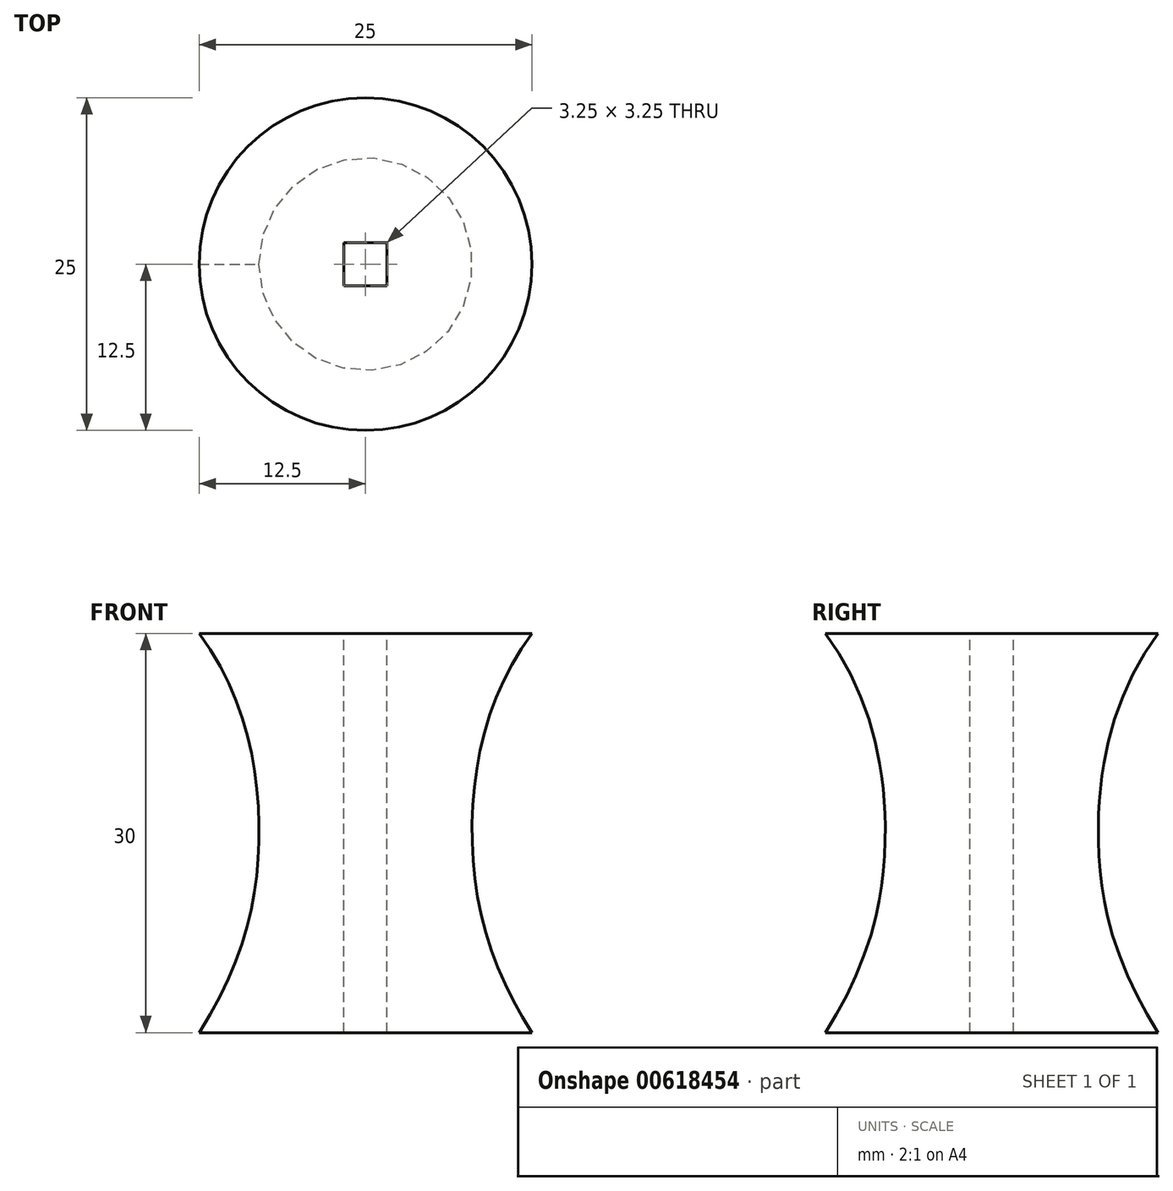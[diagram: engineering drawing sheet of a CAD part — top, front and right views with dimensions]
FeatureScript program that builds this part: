
annotation { "Feature Type Name" : "Feature", "Feature Type Description" : "" }
export const myFeature = defineFeature(function(context is Context, id is Id, definition is map)
    precondition{}
    {
        {
            var Q0;
            Q0=qCreatedBy(makeId("Front.planeOp"),FACE);
            var sketch = newSketch(context, id + "F0", { "sketchPlane" : qUnion([Q0])});
            skLineSegment(sketch, "E0", {"start": v(0, 0) * mm, "end": v(12.5, 0) * mm});
            skLineSegment(sketch, "E1", {"start": v(0, 0) * mm, "end": v(0, 30) * mm});
            skLineSegment(sketch, "E2", {"start": v(0, 30) * mm, "end": v(12.5, 30) * mm});
            skFitSpline(sketch, "E3", {"points": [v(12.5, 30) * mm, v(8, 15) * mm, v(12.5, 0) * mm], "startDerivative": vector(-20.66, -27.96) * mm, "endDerivative": vector(20.23, -32) * mm});
            skSolve(sketch);
        }
        {
            var Q0;
            Q0=makeQuery(id+"F0.imprint","IMPRINT",FACE,{"disambiguationData":[TD([[makeQuery(id+"F0.imprint","IMPRINT",EDGE,{"derivedFrom":sQuery(id+"F0.wireOp",EDGE,"E0")}),1.0]])]});
            var Q1;
            Q1=sQuery(id+"F0.wireOp",EDGE,"E1");
            revolve(context, id + "F1", {"entities" : qUnion([Q0]), "axis" : qUnion([Q1]), "revolveType" : RevolveType.FULL});
        }
        {
            var Q0;
            Q0=makeQuery(id+"F1.opRevolve","SWEPT_FACE",FACE,{"disambiguationData":[OSD([sQuery(id+"F0.wireOp",EDGE,"E2")])]});
            var sketch = newSketch(context, id + "F2", { "sketchPlane" : qUnion([Q0])});
            skLineSegment(sketch, "E4.bottom", {"start": v(1.63, -1.62) * mm, "end": v(-1.63, -1.63) * mm});
            skLineSegment(sketch, "E4.top", {"start": v(1.63, 1.63) * mm, "end": v(-1.62, 1.63) * mm});
            skLineSegment(sketch, "E4.left", {"start": v(1.63, -1.62) * mm, "end": v(1.63, 1.63) * mm});
            skLineSegment(sketch, "E4.right", {"start": v(-1.62, -1.63) * mm, "end": v(-1.62, 1.63) * mm});
            skPoint(sketch, "E4.middle", {"position": v(0, 0) * mm});
            skSolve(sketch);
        }
        {
            var Q0;
            Q0=makeQuery(id+"F2.imprint","IMPRINT",FACE,{"disambiguationData":[TD([[makeQuery(id+"F2.imprint","IMPRINT",EDGE,{"derivedFrom":sQuery(id+"F2.wireOp",EDGE,"E4.bottom")}),-1.0]])]});
            extrude(context, id + "F3", {"entities" : qUnion([Q0]), "operationType" : NewBodyOperationType.REMOVE, "endBound" : BoundingType.THROUGH_ALL, "oppositeDirection" : true, "depth" : 25 * mm, "offsetDistance" : 25 * mm});
        }
    });
